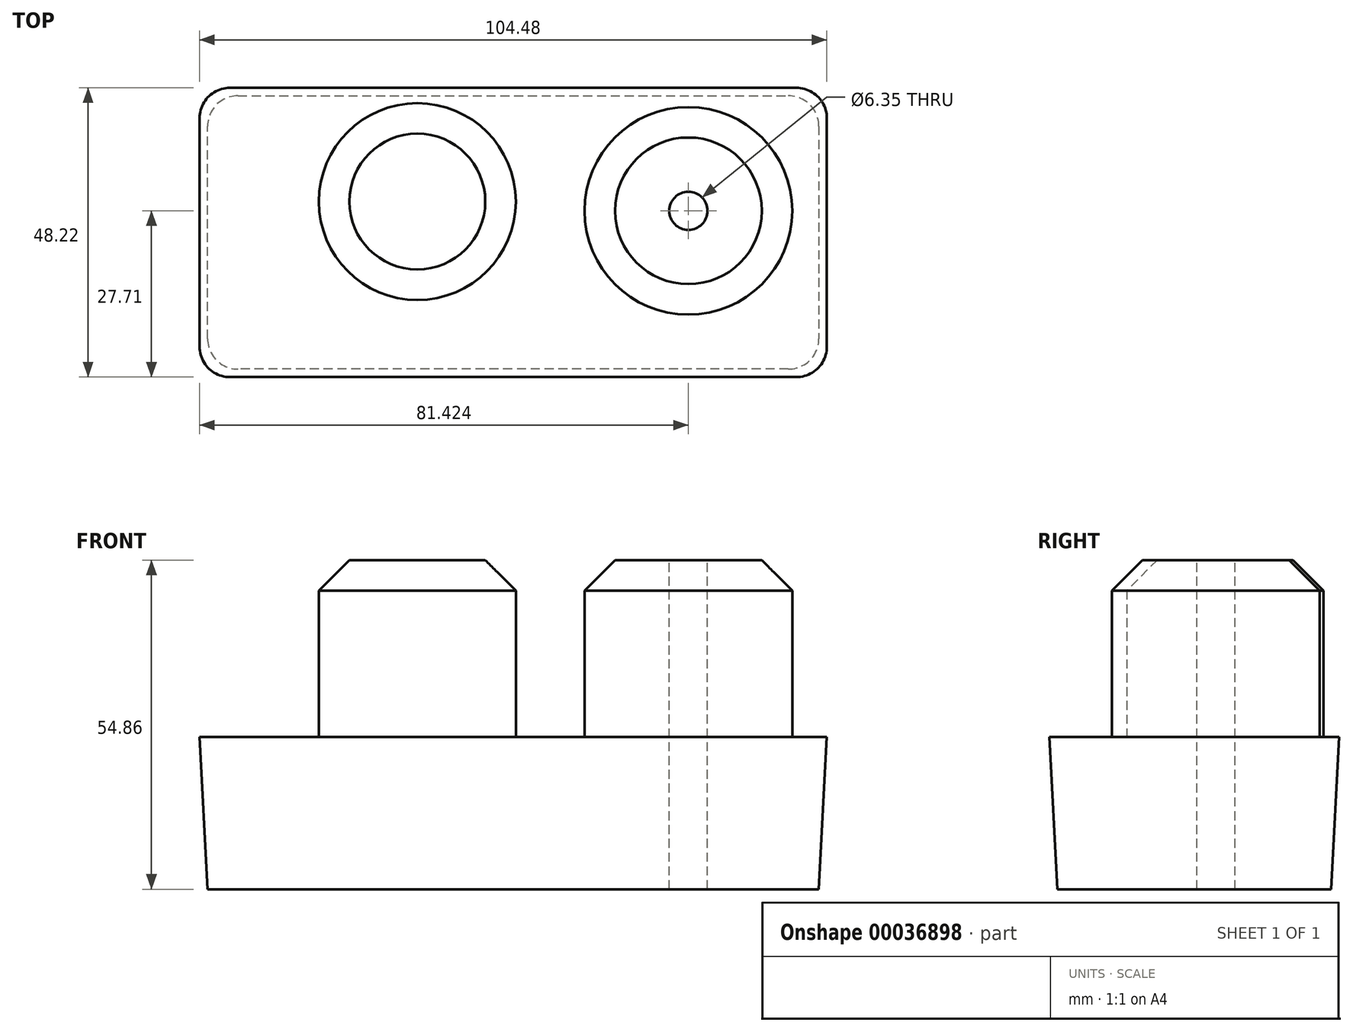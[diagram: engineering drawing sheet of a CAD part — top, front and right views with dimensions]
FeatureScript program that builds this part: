
annotation { "Feature Type Name" : "Feature", "Feature Type Description" : "" }
export const myFeature = defineFeature(function(context is Context, id is Id, definition is map)
    precondition{}
    {
        {
            var Q0;
            Q0=qCreatedBy(makeId("Top.planeOp"),FACE);
            var sketch = newSketch(context, id + "F0", { "sketchPlane" : qUnion([Q0])});
            skLineSegment(sketch, "E0.bottom", {"start": v(-101.82, 45.56) * mm, "end": v(0, 45.56) * mm});
            skLineSegment(sketch, "E0.top", {"start": v(-101.82, 0) * mm, "end": v(0, 0) * mm});
            skLineSegment(sketch, "E0.left", {"start": v(-101.82, 45.56) * mm, "end": v(-101.82, 0) * mm});
            skLineSegment(sketch, "E0.right", {"start": v(0, 45.56) * mm, "end": v(0, 0) * mm});
            skSolve(sketch);
        }
        {
            var Q0;
            Q0=makeQuery(id+"F0.imprint","IMPRINT",FACE,{"disambiguationData":[TD([[makeQuery(id+"F0.imprint","IMPRINT",EDGE,{"derivedFrom":sQuery(id+"F0.wireOp",EDGE,"E0.bottom")}),-1.0]])]});
            extrude(context, id + "F1", {"entities" : qUnion([Q0]), "depth" : 25.4 * mm, "hasDraft" : true, "draftAngle" : 3 * degree});
        }
        {
            var Q0;
            Q0=makeQuery(id+"F1.opExtrude","CAP_FACE",FACE,{"disambiguationData":[OSD([sQuery(id+"F0.wireOp",EDGE,"E0.bottom"),sQuery(id+"F0.wireOp",EDGE,"E0.top"),sQuery(id+"F0.wireOp",EDGE,"E0.left"),sQuery(id+"F0.wireOp",EDGE,"E0.right")])],"isStart":false});
            var sketch = newSketch(context, id + "F2", { "sketchPlane" : qUnion([Q0])});
            skCircle(sketch, "E1", {"center": v(-66.87, 27.92) * mm, "radius": 16.4 * mm});
            skCircle(sketch, "E2", {"center": v(-21.73, 26.38) * mm, "radius": 17.3 * mm});
            skSolve(sketch);
        }
        {
            var Q0;
            Q0 = qSketchRegion(id + "F2", true);
            extrude(context, id + "F3", {"entities" : qUnion([Q0]), "operationType" : NewBodyOperationType.ADD, "depth" : 29.46 * mm});
        }
        {
            var Q0;
            Q0=makeQuery(id+"F1.opExtrude","SWEPT_EDGE",EDGE,{"disambiguationData":[OSD([sQuery(id+"F0.wireOp",EDGE,"E0.top"),sQuery(id+"F0.wireOp",EDGE,"E0.left")])]});
            var Q1;
            Q1=makeQuery(id+"F1.opExtrude","SWEPT_EDGE",EDGE,{"disambiguationData":[OSD([sQuery(id+"F0.wireOp",EDGE,"E0.top"),sQuery(id+"F0.wireOp",EDGE,"E0.right")])]});
            var Q2;
            Q2=makeQuery(id+"F1.opExtrude","SWEPT_EDGE",EDGE,{"disambiguationData":[OSD([sQuery(id+"F0.wireOp",EDGE,"E0.bottom"),sQuery(id+"F0.wireOp",EDGE,"E0.right")])]});
            var Q3;
            Q3=makeQuery(id+"F1.opExtrude","SWEPT_EDGE",EDGE,{"disambiguationData":[OSD([sQuery(id+"F0.wireOp",EDGE,"E0.bottom"),sQuery(id+"F0.wireOp",EDGE,"E0.left")])]});
            fillet(context, id + "F4", {"entities" : qUnion([Q0, Q1, Q2, Q3]), "radius" : 5.08 * mm, "tangentPropagation" : true, "allowEdgeOverflow" : false});
        }
        {
            var Q0;
            Q0=makeQuery(id+"F3.opExtrude","CAP_EDGE",EDGE,{"disambiguationData":[OSD([sQuery(id+"F2.wireOp",EDGE,"E2")])],"isStart":false});
            var Q1;
            Q1=makeQuery(id+"F3.opExtrude","CAP_EDGE",EDGE,{"disambiguationData":[OSD([sQuery(id+"F2.wireOp",EDGE,"E1")])],"isStart":false});
            chamfer(context, id + "F5", {"entities" : qUnion([Q0, Q1]), "width" : 5.08 * mm, "tangentPropagation" : true});
        }
        {
            var Q0;
            Q0=makeQuery(id+"F3.opExtrude","CAP_FACE",FACE,{"disambiguationData":[OSD([sQuery(id+"F2.wireOp",EDGE,"E2")])],"isStart":false});
            var sketch = newSketch(context, id + "F6", { "sketchPlane" : qUnion([Q0])});
            skPoint(sketch, "E3", {"position": v(-21.73, 26.38) * mm});
            skSolve(sketch);
        }
        {
            var Q0;
            Q0=sQuery(id+"F6.wireOp",VERTEX,"E3");
            var Q1;
            Q1=makeQuery(id+"F1.opExtrude","SWEPT_BODY",BODY,{"disambiguationData":[OSD([sQuery(id+"F0.wireOp",EDGE,"E0.bottom"),sQuery(id+"F0.wireOp",EDGE,"E0.top"),sQuery(id+"F0.wireOp",EDGE,"E0.left"),sQuery(id+"F0.wireOp",EDGE,"E0.right")])]});
            hole(context, id + "F7", {"style" : HoleStyle.SIMPLE, "holeDiameter" : 6.35 * mm, "endStyle" : HoleEndStyle.THROUGH, "locations" : qUnion([Q0]), "scope" : qUnion([Q1])});
        }
    });
